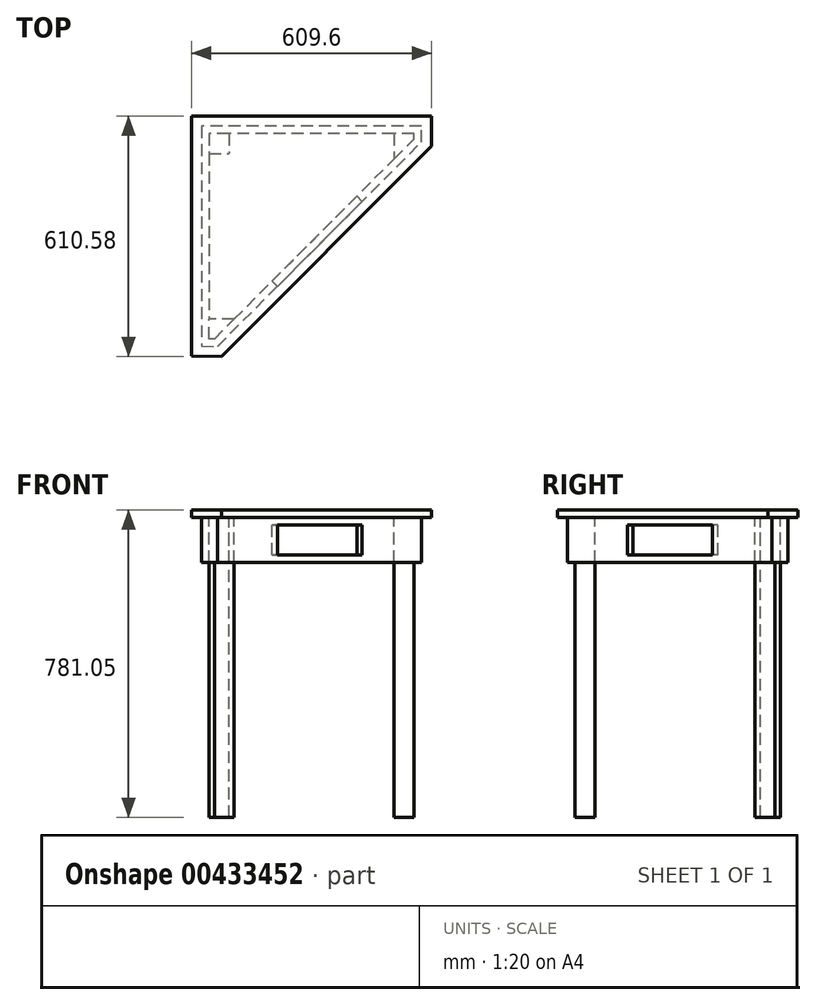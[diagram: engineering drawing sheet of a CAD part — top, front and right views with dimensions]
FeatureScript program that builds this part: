
annotation { "Feature Type Name" : "Feature", "Feature Type Description" : "" }
export const myFeature = defineFeature(function(context is Context, id is Id, definition is map)
    precondition{}
    {
        {
            var Q0;
            Q0=qCreatedBy(makeId("Top.planeOp"),FACE);
            var sketch = newSketch(context, id + "F0", { "sketchPlane" : qUnion([Q0])});
            skLineSegment(sketch, "E0", {"start": v(0, 0) * mm, "end": v(0, -609.6) * mm});
            skLineSegment(sketch, "E1", {"start": v(0, -609.6) * mm, "end": v(76.2, -610.58) * mm});
            skLineSegment(sketch, "E2", {"start": v(76.2, -610.58) * mm, "end": v(609.6, -76.2) * mm});
            skLineSegment(sketch, "E3", {"start": v(609.6, -76.2) * mm, "end": v(609.6, 0) * mm});
            skLineSegment(sketch, "E4", {"start": v(609.6, 0) * mm, "end": v(0, 0) * mm});
            skSolve(sketch);
        }
        {
            var Q0;
            Q0 = qSketchRegion(id + "F0", true);
            extrude(context, id + "F1", {"entities" : qUnion([Q0]), "depth" : 19.05 * mm});
        }
        {
            var Q0;
            Q0=makeQuery(id+"F1.opExtrude","CAP_FACE",FACE,{"disambiguationData":[OSD([sQuery(id+"F0.wireOp",EDGE,"E0"),sQuery(id+"F0.wireOp",EDGE,"E1"),sQuery(id+"F0.wireOp",EDGE,"E2"),sQuery(id+"F0.wireOp",EDGE,"E3"),sQuery(id+"F0.wireOp",EDGE,"E4")])],"isStart":true});
            var sketch = newSketch(context, id + "F2", { "sketchPlane" : qUnion([Q0])});
            skLineSegment(sketch, "E5.0", {"start": v(25.4, 584.53) * mm, "end": v(65.8, 585.05) * mm});
            skLineSegment(sketch, "E5.1", {"start": v(25.4, 25.4) * mm, "end": v(25.4, 584.53) * mm});
            skLineSegment(sketch, "E5.2", {"start": v(65.8, 585.05) * mm, "end": v(584.2, 65.7) * mm});
            skLineSegment(sketch, "E5.3", {"start": v(584.2, 65.7) * mm, "end": v(584.2, 25.4) * mm});
            skLineSegment(sketch, "E5.4", {"start": v(584.2, 25.4) * mm, "end": v(25.4, 25.4) * mm});
            skSolve(sketch);
        }
        {
            var Q0;
            Q0=makeQuery(id+"F2.imprint","IMPRINT",FACE,{"disambiguationData":[TD([[makeQuery(id+"F2.imprint","IMPRINT",EDGE,{"derivedFrom":sQuery(id+"F2.wireOp",EDGE,"E5.0")}),-1.0]])]});
            var sketch = newSketch(context, id + "F3", { "sketchPlane" : qUnion([Q0])});
            skLineSegment(sketch, "E6.0", {"start": v(44.45, 565.72) * mm, "end": v(58, 565.9) * mm});
            skLineSegment(sketch, "E6.1", {"start": v(44.45, 44.45) * mm, "end": v(44.45, 565.72) * mm});
            skLineSegment(sketch, "E6.2", {"start": v(58, 565.9) * mm, "end": v(565.15, 57.81) * mm});
            skLineSegment(sketch, "E6.3", {"start": v(565.15, 57.81) * mm, "end": v(565.15, 44.45) * mm});
            skLineSegment(sketch, "E6.4", {"start": v(565.15, 44.45) * mm, "end": v(44.45, 44.45) * mm});
            skPoint(sketch, "E7", {"position": v(311.57, 311.85) * mm});
            skSolve(sketch);
        }
        {
            var Q0;
            Q0=makeQuery(id+"F3.imprint","IMPRINT",FACE,{"disambiguationData":[TD([[makeQuery(id+"F3.imprint","IMPRINT",EDGE,{"derivedFrom":sQuery(id+"F3.wireOp",EDGE,"E6.0")}),1.0]])]});
            extrude(context, id + "F4", {"entities" : qUnion([Q0]), "operationType" : NewBodyOperationType.ADD, "depth" : 114.3 * mm});
        }
        {
            var Q0;
            Q0=makeQuery(id+"F4.opExtrude","SWEPT_FACE",FACE,{"disambiguationData":[OSD([sQuery(id+"F2.wireOp",EDGE,"E5.2")])]});
            var sketch = newSketch(context, id + "F5", { "sketchPlane" : qUnion([Q0])});
            skLineSegment(sketch, "E8.bottom", {"start": v(152.4, -95.25) * mm, "end": v(-152.4, -95.25) * mm});
            skLineSegment(sketch, "E8.top", {"start": v(152.4, -19.05) * mm, "end": v(-152.4, -19.05) * mm});
            skLineSegment(sketch, "E8.left", {"start": v(152.4, -95.25) * mm, "end": v(152.4, -19.05) * mm});
            skLineSegment(sketch, "E8.right", {"start": v(-152.4, -95.25) * mm, "end": v(-152.4, -19.05) * mm});
            skPoint(sketch, "E8.middle", {"position": v(0, -57.15) * mm});
            skSolve(sketch);
        }
        {
            var Q0;
            Q0 = qSketchRegion(id + "F5", true);
            extrude(context, id + "F6", {"entities" : qUnion([Q0]), "operationType" : NewBodyOperationType.REMOVE, "oppositeDirection" : true, "depth" : 205.1 * mm});
        }
        {
            var Q0;
            Q0=makeQuery(id+"F2.imprint","IMPRINT",FACE,{"disambiguationData":[TD([[makeQuery(id+"F2.imprint","IMPRINT",EDGE,{"derivedFrom":sQuery(id+"F2.wireOp",EDGE,"E5.0")}),-1.0]])]});
            var sketch = newSketch(context, id + "F7", { "sketchPlane" : qUnion([Q0])});
            skLineSegment(sketch, "E9", {"start": v(44.45, 565.9) * mm, "end": v(58, 565.9) * mm});
            skLineSegment(sketch, "E10", {"start": v(58, 565.9) * mm, "end": v(107.89, 515.92) * mm});
            skLineSegment(sketch, "E11", {"start": v(107.89, 515.92) * mm, "end": v(44.45, 515.1) * mm});
            skLineSegment(sketch, "E12", {"start": v(44.45, 515.1) * mm, "end": v(44.45, 565.9) * mm});
            skSolve(sketch);
        }
        {
            var Q0;
            Q0 = qSketchRegion(id + "F7", true);
            extrude(context, id + "F8", {"entities" : qUnion([Q0]), "operationType" : NewBodyOperationType.ADD, "depth" : 762 * mm});
        }
        {
            var Q0;
            Q0=makeQuery(id+"F2.imprint","IMPRINT",FACE,{"disambiguationData":[TD([[makeQuery(id+"F2.imprint","IMPRINT",EDGE,{"derivedFrom":sQuery(id+"F2.wireOp",EDGE,"E5.0")}),-1.0]])]});
            var sketch = newSketch(context, id + "F9", { "sketchPlane" : qUnion([Q0])});
            skLineSegment(sketch, "E13", {"start": v(565.15, 57.81) * mm, "end": v(565.15, 44.45) * mm});
            skLineSegment(sketch, "E14", {"start": v(565.15, 44.45) * mm, "end": v(514.35, 44.45) * mm});
            skLineSegment(sketch, "E15", {"start": v(514.35, 44.45) * mm, "end": v(514.35, 108.7) * mm});
            skLineSegment(sketch, "E16", {"start": v(514.35, 108.7) * mm, "end": v(565.15, 57.81) * mm});
            skSolve(sketch);
        }
        {
            var Q0;
            Q0 = qSketchRegion(id + "F9", true);
            extrude(context, id + "F10", {"entities" : qUnion([Q0]), "operationType" : NewBodyOperationType.ADD, "depth" : 762 * mm});
        }
        {
            var Q0;
            Q0=makeQuery(id+"F2.imprint","IMPRINT",FACE,{"disambiguationData":[TD([[makeQuery(id+"F2.imprint","IMPRINT",EDGE,{"derivedFrom":sQuery(id+"F2.wireOp",EDGE,"E5.0")}),-1.0]])]});
            var sketch = newSketch(context, id + "F11", { "sketchPlane" : qUnion([Q0])});
            skLineSegment(sketch, "E17.bottom", {"start": v(44.45, 44.45) * mm, "end": v(95.25, 44.45) * mm});
            skLineSegment(sketch, "E17.top", {"start": v(44.45, 95.25) * mm, "end": v(95.25, 95.25) * mm});
            skLineSegment(sketch, "E17.left", {"start": v(44.45, 44.45) * mm, "end": v(44.45, 95.25) * mm});
            skLineSegment(sketch, "E17.right", {"start": v(95.25, 44.45) * mm, "end": v(95.25, 95.25) * mm});
            skSolve(sketch);
        }
        {
            var Q0;
            Q0=makeQuery(id+"F11.imprint","IMPRINT",FACE,{"disambiguationData":[TD([[makeQuery(id+"F11.imprint","IMPRINT",EDGE,{"derivedFrom":sQuery(id+"F11.wireOp",EDGE,"E17.bottom")}),1.0]])]});
            extrude(context, id + "F12", {"entities" : qUnion([Q0]), "operationType" : NewBodyOperationType.ADD, "depth" : 762 * mm});
        }
    });
